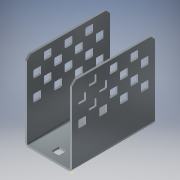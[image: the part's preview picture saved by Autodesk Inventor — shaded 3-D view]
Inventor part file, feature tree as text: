
AUTODESK INVENTOR PART (.ipt)
format: ipt  version: 2018 (Build 220112000, 112)  size: 676,352 bytes
history: native  units: in
note: dims shown in document units (in); Inventor stores cm internally (conversion verified against a paired STEP export)
features: other x37, extrude x32, sketch x8, sheet_metal_op x3, pattern_linear x3, plane x2, mirror x2
ambient origin geometry x8: Origin, YZ Plane, XZ Plane, XY Plane, X Axis, Y Axis, Z Axis, Center Point
bodies: Solid1 (feature_tree)
feature tree (87):
  sheet_metal_op  "Face1"
  sheet_metal_op  "Flange1"
  other  "Corner Chamfer1"
  plane  "Work Plane1"
  mirror  "Mirror1"
  pattern_linear  "Rectangular Pattern1"  Spacing1=0.1874in  [1 undecoded]
  pattern_linear  "Rectangular Pattern2"  Spacing1=0.0469in  [1 undecoded]
  plane  "Work Plane2"
  mirror  "Mirror2"
  pattern_linear  "Rectangular Pattern3"  Spacing1=0.0469in  [1 undecoded]
  sketch  "Sketch8"  dims[d7=1.885in d8=90.0deg d9=0.0469in d10=0.1874in d11=0.0469in d12=0.0469in d13=0.1in d14=0.25in d15=45.0deg d16=0.182in d17=0.182in d18=0.02in d19=0.5in d20=0.206in d21=1.1811in d23=0.5in d24=0.3937in d26=1.0in d28=0.7874in d30=0.5in d31=0.3937in d33=1.0in d35=0.02in d36=0.25in d37=0.182in d38=0.182in d39=0.25in d40=1.5748in d42=0.5in d43=0.7874in d45=0.5in d48=0.0469in d49=0.0in d50=0.182in d51=0.182in d52=0.02in d53=0.25in d54=1.5748in d56=0.5in d57=0.3937in d59=1.0in d61=0.0469in d62=0.0in d63=1.0in d64=0.0in d65=1.1811in d67=0.5in d68=0.7874in d70=0.5in d71=1.0in d72=0.0in d73=1.5748in d75=0.5in d76=0.7874in d78=0.5in d79=1.0in d80=0.0in d81=1.5748in d83=0.5in d84=0.0in d85=0.0in d86=0.0in d87=0.0in d88=0.0in d89=0.0in d90=0.0in d91=0.0in d92=0.0in d93=0.0in d94=0.0in d95=0.0in d96=0.0in d97=0.0in d98=0.0in d99=0.0in d100=0.0in d101=0.0in d102=0.0in d103=0.0in d104=0.0in d105=0.0in d106=0.0in d107=0.0in d108=0.0in d109=0.0in d110=0.0in d111=0.0in d112=0.0in d113=0.0in d114=0.0in d115=0.0in d116=0.0in d117=0.0in d118=0.0in d119=0.0in d120=0.0in d121=0.0in d122=0.0in d123=0.0in d124=0.0in d125=0.0in d126=0.0in d127=0.0in d128=0.0in d129=0.0in d130=0.0in d131=0.0in d132=0.0in d133=0.0in d134=0.0in d135=0.0in d136=0.0in d137=0.0in d138=0.0in d139=0.0in d140=0.0in d141=0.0in d142=0.0in d143=0.0in d144=0.0in d145=0.0in d146=0.0in d147=0.0in d148=0.0469in]
  sketch  "Sketch1"  dims[d0=2.0in]
  other  "Plate1"
  sketch  "Sketch2"  dims[d1=1.129in]
  other  "Plate2"
  sheet_metal_op  "Bend1"
  sketch  "Sketch3"  dims[d2=0.0469in]
  sketch  "Sketch4"  dims[d3=0.0469in]
  sketch  "Sketch5"  dims[d4=0.0234in]
  other  "Srf1"
  other  "Srf2"
  other  "Srf3"
  other  "Srf4"
  other  "Srf5"
  other  "Srf6"
  sketch  "Sketch6"  dims[d5=0.0937in]
  other  "Srf7"
  other  "Srf8"
  other  "Srf9"
  other  "Srf10"
  other  "Srf11"
  other  "Srf12"
  other  "Srf13"
  other  "Srf14"
  other  "Srf18"
  other  "Srf19"
  other  "Srf20"
  other  "Srf15"
  other  "Srf16"
  other  "Srf17"
  other  "Srf21"
  other  "Srf22"
  other  "Srf23"
  other  "Srf24"
  other  "Srf25"
  other  "Srf26"
  other  "Srf27"
  other  "Srf28"
  sketch  "Sketch7"  dims[d6=0.0469in]
  other  "Srf29"
  other  "Srf30"
  other  "Srf31"
  other  "Srf32"
  other  "Cut1"
  other  "Cut2"
  extrude  "ExtrusionSrf1"  Depth=0.25in TaperAngle=45.0deg
  extrude  "ExtrusionSrf7"  Depth=0.182in
  extrude  "ExtrusionSrf29"  Depth=0.182in
  extrude  "ExtrusionSrf2"  Depth=0.02in
  extrude  "ExtrusionSrf3"  Depth=0.5in
  extrude  "ExtrusionSrf4"  Depth=0.0469in
  extrude  "ExtrusionSrf5"  Depth=0.5in
  extrude  "ExtrusionSrf6"  Depth=0.5in
  extrude  "ExtrusionSrf8"  Depth=0.02in
  extrude  "ExtrusionSrf9"  Depth=0.25in
  extrude  "ExtrusionSrf10"  Depth=0.182in
  extrude  "ExtrusionSrf11"  Depth=0.182in
  extrude  "ExtrusionSrf12"  Depth=0.25in
  extrude  "ExtrusionSrf13"  Depth=0.5in
  extrude  "ExtrusionSrf14"  Depth=0.0469in
  extrude  "ExtrusionSrf15"  TaperAngle=0.0deg  [1 undecoded]
  extrude  "ExtrusionSrf16"  Depth=0.182in
  extrude  "ExtrusionSrf17"  Depth=0.182in
  extrude  "ExtrusionSrf18"  Depth=0.02in
  extrude  "ExtrusionSrf19"  Depth=0.25in
  extrude  "ExtrusionSrf20"  Depth=0.5in
  extrude  "ExtrusionSrf21"  Depth=0.0469in
  extrude  "ExtrusionSrf22"  TaperAngle=0.0deg  [1 undecoded]
  extrude  "ExtrusionSrf23"  Depth=1.0in TaperAngle=0.0deg
  extrude  "ExtrusionSrf24"  Depth=0.5in
  extrude  "ExtrusionSrf25"  Depth=0.5in
  extrude  "ExtrusionSrf26"  Depth=1.0in TaperAngle=0.0deg
  extrude  "ExtrusionSrf27"  Depth=0.5in
  extrude  "ExtrusionSrf28"  Depth=0.5in
  extrude  "ExtrusionSrf30"  Depth=1.0in TaperAngle=0.0deg
  extrude  "ExtrusionSrf31"  Depth=0.5in
  extrude  "ExtrusionSrf32"  TaperAngle=0.0deg  [1 undecoded]
note: 6 required parameter values undecoded (feature->parameter linkage not recoverable at this tier; creation-order binding heuristic only, values carry confidence <= 0.55)
